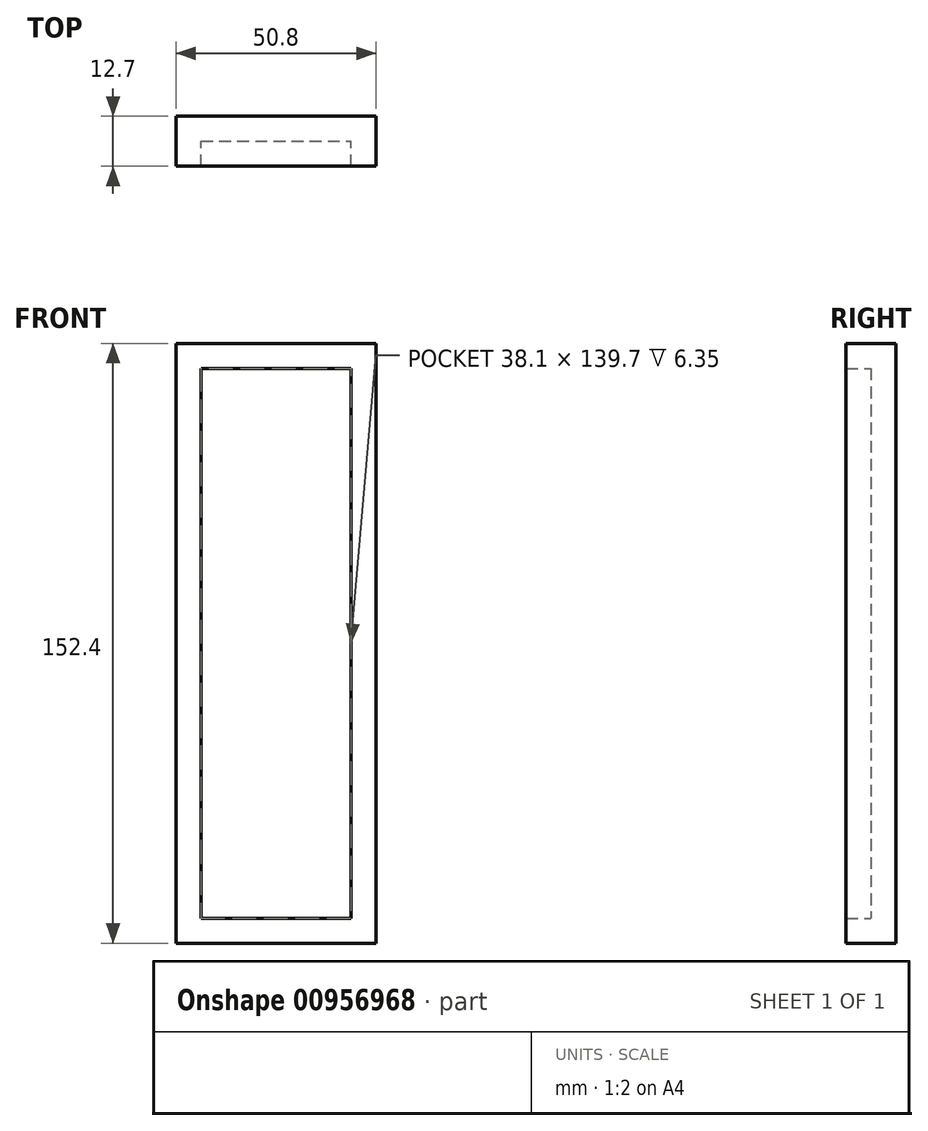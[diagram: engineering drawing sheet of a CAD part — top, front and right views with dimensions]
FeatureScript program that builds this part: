
annotation { "Feature Type Name" : "Feature", "Feature Type Description" : "" }
export const myFeature = defineFeature(function(context is Context, id is Id, definition is map)
    precondition{}
    {
        {
            var Q0;
            Q0=qCreatedBy(makeId("Front.planeOp"),FACE);
            var sketch = newSketch(context, id + "F0", { "sketchPlane" : qUnion([Q0])});
            skLineSegment(sketch, "E0.bottom", {"start": v(-65.8, 139.82) * mm, "end": v(-15, 139.82) * mm});
            skLineSegment(sketch, "E0.top", {"start": v(-65.8, -12.58) * mm, "end": v(-15, -12.58) * mm});
            skLineSegment(sketch, "E0.left", {"start": v(-65.8, 139.82) * mm, "end": v(-65.8, -12.58) * mm});
            skLineSegment(sketch, "E0.right", {"start": v(-15, 139.82) * mm, "end": v(-15, -12.58) * mm});
            skLineSegment(sketch, "E1.0", {"start": v(-59.45, 133.47) * mm, "end": v(-59.45, -6.23) * mm});
            skLineSegment(sketch, "E1.1", {"start": v(-59.45, 133.47) * mm, "end": v(-21.35, 133.47) * mm});
            skLineSegment(sketch, "E1.2", {"start": v(-21.35, 133.47) * mm, "end": v(-21.35, -6.23) * mm});
            skLineSegment(sketch, "E1.3", {"start": v(-59.45, -6.23) * mm, "end": v(-21.35, -6.23) * mm});
            skSolve(sketch);
        }
        {
            var Q0;
            Q0=makeQuery(id+"F0.imprint","IMPRINT",FACE,{"disambiguationData":[TD([[makeQuery(id+"F0.imprint","IMPRINT",EDGE,{"derivedFrom":sQuery(id+"F0.wireOp",EDGE,"E0.bottom")}),-1.0]])]});
            extrude(context, id + "F1", {"entities" : qUnion([Q0]), "depth" : 6.35 * mm, "offsetDistance" : 25.4 * mm});
        }
        {
            var Q0;
            Q0=makeQuery(id+"F1.opExtrude","CAP_FACE",FACE,{"disambiguationData":[OSD([sQuery(id+"F0.wireOp",EDGE,"E0.bottom"),sQuery(id+"F0.wireOp",EDGE,"E0.top"),sQuery(id+"F0.wireOp",EDGE,"E0.left"),sQuery(id+"F0.wireOp",EDGE,"E0.right"),sQuery(id+"F0.wireOp",EDGE,"E1.0"),sQuery(id+"F0.wireOp",EDGE,"E1.1"),sQuery(id+"F0.wireOp",EDGE,"E1.2"),sQuery(id+"F0.wireOp",EDGE,"E1.3")])],"isStart":true});
            var sketch = newSketch(context, id + "F2", { "sketchPlane" : qUnion([Q0])});
            skLineSegment(sketch, "E2.bottom", {"start": v(15, 139.82) * mm, "end": v(65.8, 139.82) * mm});
            skLineSegment(sketch, "E2.top", {"start": v(15, -12.58) * mm, "end": v(65.8, -12.58) * mm});
            skLineSegment(sketch, "E2.left", {"start": v(15, 139.82) * mm, "end": v(15, -12.58) * mm});
            skLineSegment(sketch, "E2.right", {"start": v(65.8, 139.82) * mm, "end": v(65.8, -12.58) * mm});
            skSolve(sketch);
        }
        {
            var Q0;
            Q0 = qSketchRegion(id + "F2", true);
            extrude(context, id + "F3", {"entities" : qUnion([Q0]), "operationType" : NewBodyOperationType.ADD, "depth" : 6.35 * mm, "offsetDistance" : 25.4 * mm});
        }
    });
